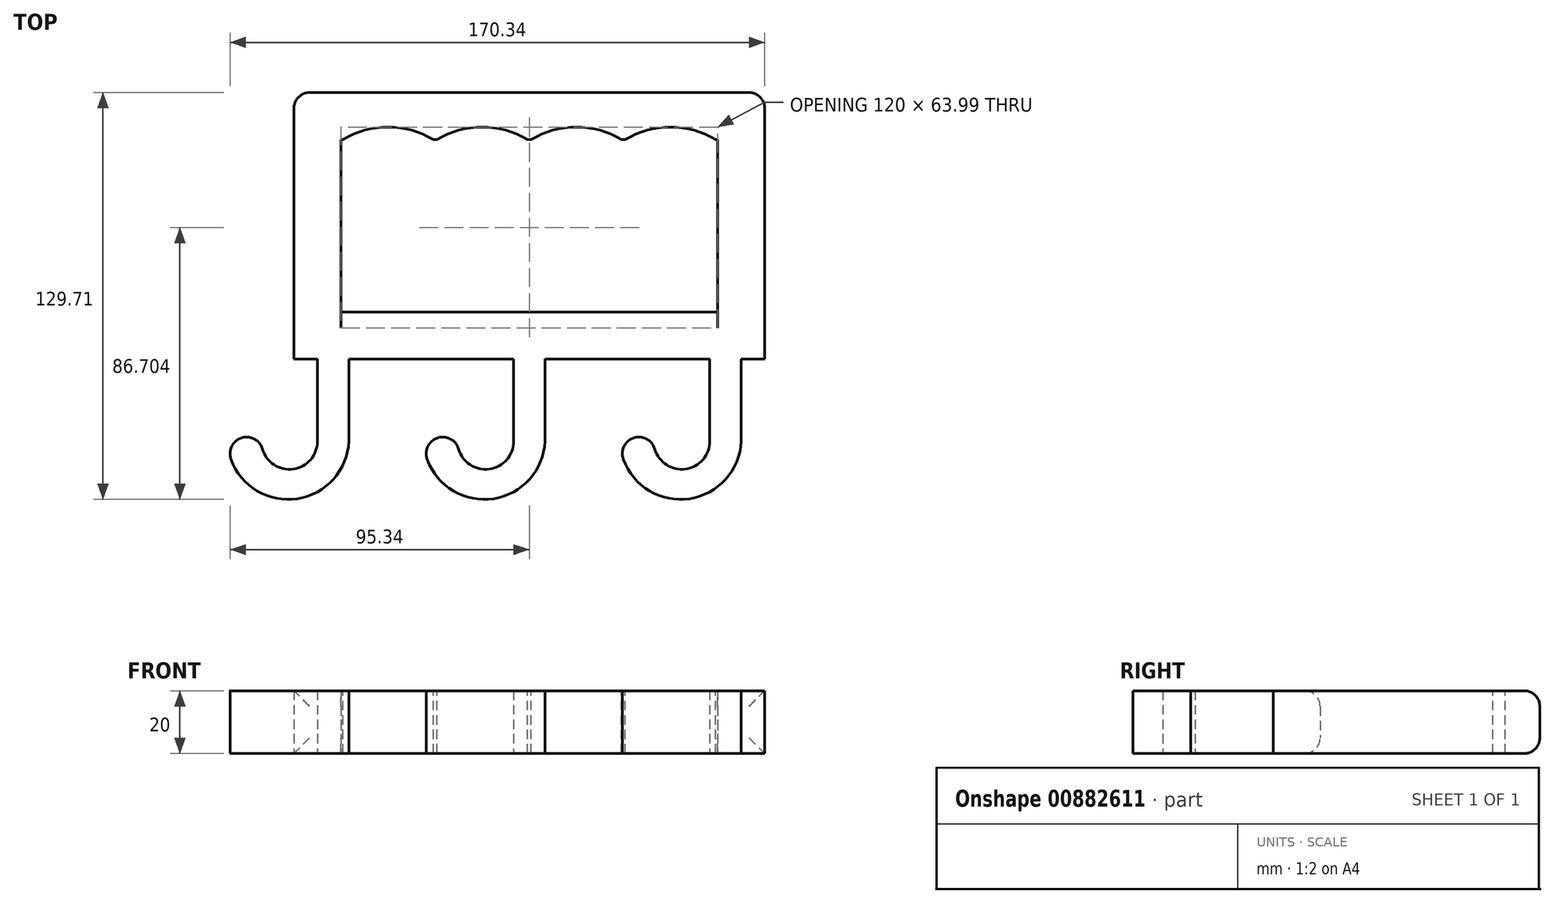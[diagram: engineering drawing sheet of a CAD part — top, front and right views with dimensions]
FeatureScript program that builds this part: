
annotation { "Feature Type Name" : "Feature", "Feature Type Description" : "" }
export const myFeature = defineFeature(function(context is Context, id is Id, definition is map)
    precondition{}
    {
        {
            var Q0;
            Q0=qCreatedBy(makeId("Top.planeOp"),FACE);
            var sketch = newSketch(context, id + "F0", { "sketchPlane" : qUnion([Q0])});
            skLineSegment(sketch, "E0.bottom", {"start": v(60, 27.5) * mm, "end": v(-60, 27.5) * mm});
            skLineSegment(sketch, "E0.top", {"start": v(60, -27.5) * mm, "end": v(-60, -27.5) * mm});
            skLineSegment(sketch, "E0.left", {"start": v(60, 27.5) * mm, "end": v(60, -27.5) * mm});
            skLineSegment(sketch, "E0.right", {"start": v(-60, 27.5) * mm, "end": v(-60, -27.5) * mm});
            skPoint(sketch, "E0.middle", {"position": v(0, 0) * mm});
            skLineSegment(sketch, "E1.bottom", {"start": v(75, 42.5) * mm, "end": v(-75, 42.5) * mm});
            skLineSegment(sketch, "E1.top", {"start": v(75, -42.5) * mm, "end": v(-75, -42.5) * mm});
            skLineSegment(sketch, "E1.left", {"start": v(75, 42.5) * mm, "end": v(75, -42.5) * mm});
            skLineSegment(sketch, "E1.right", {"start": v(-75, 42.5) * mm, "end": v(-75, -42.5) * mm});
            skLineSegment(sketch, "E2", {"start": v(-67.5, -42.5) * mm, "end": v(-67.5, -68.7) * mm});
            skArc(sketch, "E3", {"start": v(-85.02, -71.15) * mm, "mid": v(-75.2, -77.54) * mm, "end": v(-67.5, -68.7) * mm});
            skArc(sketch, "E4", {"start": v(-85.02, -71.15) * mm, "mid": v(-91.7, -67.6) * mm, "end": v(-95.04, -74.37) * mm});
            skArc(sketch, "E5", {"start": v(-95.04, -74.37) * mm, "mid": v(-73.93, -87) * mm, "end": v(-57.5, -68.7) * mm});
            skLineSegment(sketch, "E6", {"start": v(-57.5, -68.7) * mm, "end": v(-57.5, -42.5) * mm});
            skLineSegment(sketch, "E7.1.0.0", {"start": v(5, -68.7) * mm, "end": v(5, -42.5) * mm});
            skArc(sketch, "E7.1.0.1", {"start": v(-32.54, -74.37) * mm, "mid": v(-11.43, -87) * mm, "end": v(5, -68.7) * mm});
            skArc(sketch, "E7.1.0.2", {"start": v(-22.52, -71.15) * mm, "mid": v(-29.2, -67.6) * mm, "end": v(-32.54, -74.37) * mm});
            skArc(sketch, "E7.1.0.3", {"start": v(-22.52, -71.15) * mm, "mid": v(-12.7, -77.54) * mm, "end": v(-5, -68.7) * mm});
            skLineSegment(sketch, "E7.1.0.4", {"start": v(-5, -42.5) * mm, "end": v(-5, -68.7) * mm});
            skLineSegment(sketch, "E7.2.0.0", {"start": v(67.5, -68.7) * mm, "end": v(67.5, -42.5) * mm});
            skArc(sketch, "E7.2.0.1", {"start": v(29.96, -74.37) * mm, "mid": v(51.07, -87) * mm, "end": v(67.5, -68.7) * mm});
            skArc(sketch, "E7.2.0.2", {"start": v(39.98, -71.15) * mm, "mid": v(33.3, -67.6) * mm, "end": v(29.96, -74.37) * mm});
            skArc(sketch, "E7.2.0.3", {"start": v(39.98, -71.15) * mm, "mid": v(49.8, -77.54) * mm, "end": v(57.5, -68.7) * mm});
            skLineSegment(sketch, "E7.2.0.4", {"start": v(57.5, -42.5) * mm, "end": v(57.5, -68.7) * mm});
            skLineSegment(sketch, "E7.direction1", {"start": v(-57.5, -68.7) * mm, "end": v(5, -68.7) * mm, "construction": true});
            skSolve(sketch);
        }
        {
            var Q0;
            Q0 = qSketchRegion(id + "F0", true);
            extrude(context, id + "F1", {"entities" : qUnion([Q0]), "depth" : 20 * mm, "offsetDistance" : 25 * mm});
        }
        {
            var Q0;
            Q0=makeQuery(id+"F1.opExtrude","CAP_EDGE",EDGE,{"disambiguationData":[OSD([sQuery(id+"F0.wireOp",EDGE,"E1.bottom")])],"isStart":false});
            var Q1;
            Q1=makeQuery(id+"F1.opExtrude","CAP_EDGE",EDGE,{"disambiguationData":[OSD([sQuery(id+"F0.wireOp",EDGE,"E1.bottom")])],"isStart":true});
            var Q2;
            Q2=makeQuery(id+"F1.opExtrude","SWEPT_EDGE",EDGE,{"disambiguationData":[OSD([sQuery(id+"F0.wireOp",EDGE,"E1.bottom"),sQuery(id+"F0.wireOp",EDGE,"E1.right")])]});
            var Q3;
            Q3=makeQuery(id+"F1.opExtrude","SWEPT_EDGE",EDGE,{"disambiguationData":[OSD([sQuery(id+"F0.wireOp",EDGE,"E1.bottom"),sQuery(id+"F0.wireOp",EDGE,"E1.left")])]});
            var Q4;
            Q4=makeQuery(id+"F1.opExtrude","CAP_EDGE",EDGE,{"disambiguationData":[OSD([sQuery(id+"F0.wireOp",EDGE,"E0.top")])],"isStart":true});
            var Q5;
            Q5=makeQuery(id+"F1.opExtrude","CAP_EDGE",EDGE,{"disambiguationData":[OSD([sQuery(id+"F0.wireOp",EDGE,"E0.top")])],"isStart":false});
            fillet(context, id + "F2", {"entities" : qUnion([Q0, Q1, Q2, Q3, Q4, Q5]), "radius" : 5 * mm, "tangentPropagation" : true, "allowEdgeOverflow" : false});
        }
        {
            var Q0;
            Q0=makeQuery(id+"F1.opExtrude","CAP_FACE",FACE,{"disambiguationData":[OSD([sQuery(id+"F0.wireOp",EDGE,"E0.bottom"),sQuery(id+"F0.wireOp",EDGE,"E0.top"),sQuery(id+"F0.wireOp",EDGE,"E0.left"),sQuery(id+"F0.wireOp",EDGE,"E0.right"),sQuery(id+"F0.wireOp",EDGE,"E1.bottom"),sQuery(id+"F0.wireOp",EDGE,"E1.top"),sQuery(id+"F0.wireOp",EDGE,"E1.left"),sQuery(id+"F0.wireOp",EDGE,"E1.right"),sQuery(id+"F0.wireOp",EDGE,"E2"),sQuery(id+"F0.wireOp",EDGE,"E3"),sQuery(id+"F0.wireOp",EDGE,"E4"),sQuery(id+"F0.wireOp",EDGE,"E5"),sQuery(id+"F0.wireOp",EDGE,"E6"),sQuery(id+"F0.wireOp",EDGE,"E7.1.0.0"),sQuery(id+"F0.wireOp",EDGE,"E7.1.0.1"),sQuery(id+"F0.wireOp",EDGE,"E7.1.0.2"),sQuery(id+"F0.wireOp",EDGE,"E7.1.0.3"),sQuery(id+"F0.wireOp",EDGE,"E7.1.0.4"),sQuery(id+"F0.wireOp",EDGE,"E7.2.0.0"),sQuery(id+"F0.wireOp",EDGE,"E7.2.0.1"),sQuery(id+"F0.wireOp",EDGE,"E7.2.0.2"),sQuery(id+"F0.wireOp",EDGE,"E7.2.0.3"),sQuery(id+"F0.wireOp",EDGE,"E7.2.0.4")])],"isStart":false});
            var sketch = newSketch(context, id + "F3", { "sketchPlane" : qUnion([Q0])});
            skArc(sketch, "E8", {"start": v(-30, 27.13) * mm, "mid": v(-45, 31.49) * mm, "end": v(-60, 27.13) * mm});
            skArc(sketch, "E9", {"start": v(0, 27.13) * mm, "mid": v(-15, 31.49) * mm, "end": v(-30, 27.13) * mm});
            skArc(sketch, "E10.MirrorCS", {"start": v(0, 27.13) * mm, "mid": v(15, 31.49) * mm, "end": v(30, 27.13) * mm});
            skArc(sketch, "E11.MirrorCS", {"start": v(30, 27.13) * mm, "mid": v(45, 31.49) * mm, "end": v(60, 27.13) * mm});
            skLineSegment(sketch, "E12", {"start": v(-60, 27.5) * mm, "end": v(-30, 27.13) * mm});
            skLineSegment(sketch, "E13", {"start": v(-30, 27.13) * mm, "end": v(0, 27.13) * mm});
            skLineSegment(sketch, "E14", {"start": v(0, 27.13) * mm, "end": v(30, 27.13) * mm});
            skLineSegment(sketch, "E15", {"start": v(30, 27.13) * mm, "end": v(60, 27.5) * mm});
            skSolve(sketch);
        }
        {
            var Q0;
            Q0 = qSketchRegion(id + "F3", true);
            extrude(context, id + "F4", {"entities" : qUnion([Q0]), "operationType" : NewBodyOperationType.REMOVE, "endBound" : BoundingType.THROUGH_ALL, "oppositeDirection" : true, "depth" : 25 * mm, "offsetDistance" : 25 * mm});
        }
    });
